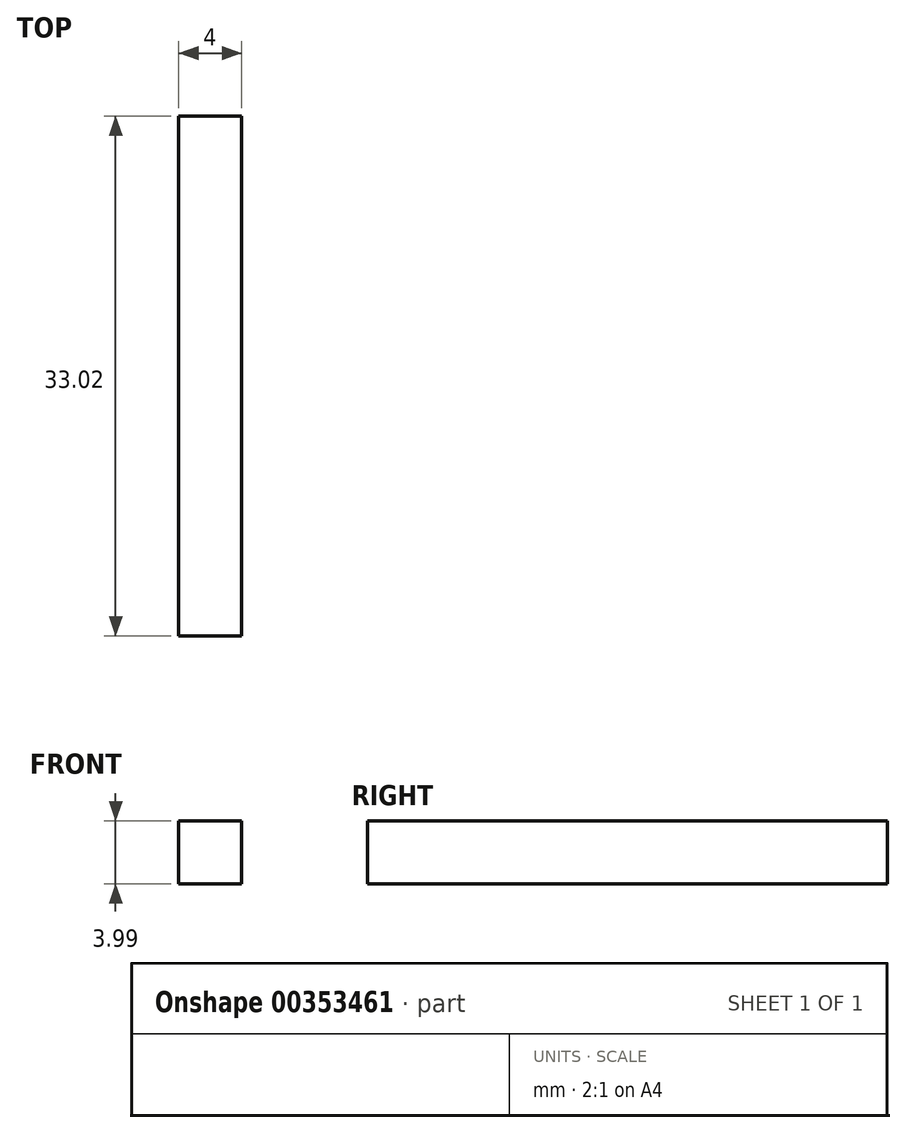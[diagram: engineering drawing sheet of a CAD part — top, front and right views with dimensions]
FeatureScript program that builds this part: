
annotation { "Feature Type Name" : "Feature", "Feature Type Description" : "" }
export const myFeature = defineFeature(function(context is Context, id is Id, definition is map)
    precondition{}
    {
        {
            var Q0;
            Q0=qCreatedBy(makeId("Front.planeOp"),FACE);
            var sketch = newSketch(context, id + "F0", { "sketchPlane" : qUnion([Q0])});
            skLineSegment(sketch, "E0.bottom", {"start": v(-44.5, 58.9) * mm, "end": v(-40.5, 58.9) * mm});
            skLineSegment(sketch, "E0.top", {"start": v(-44.5, 54.9) * mm, "end": v(-40.5, 54.9) * mm});
            skLineSegment(sketch, "E0.left", {"start": v(-44.5, 58.9) * mm, "end": v(-44.5, 54.9) * mm});
            skLineSegment(sketch, "E0.right", {"start": v(-40.5, 58.9) * mm, "end": v(-40.5, 54.9) * mm});
            skSolve(sketch);
        }
        {
            var Q0;
            Q0 = qSketchRegion(id + "F0", true);
            extrude(context, id + "F1", {"entities" : qUnion([Q0]), "depth" : 33.02 * mm});
        }
    });
